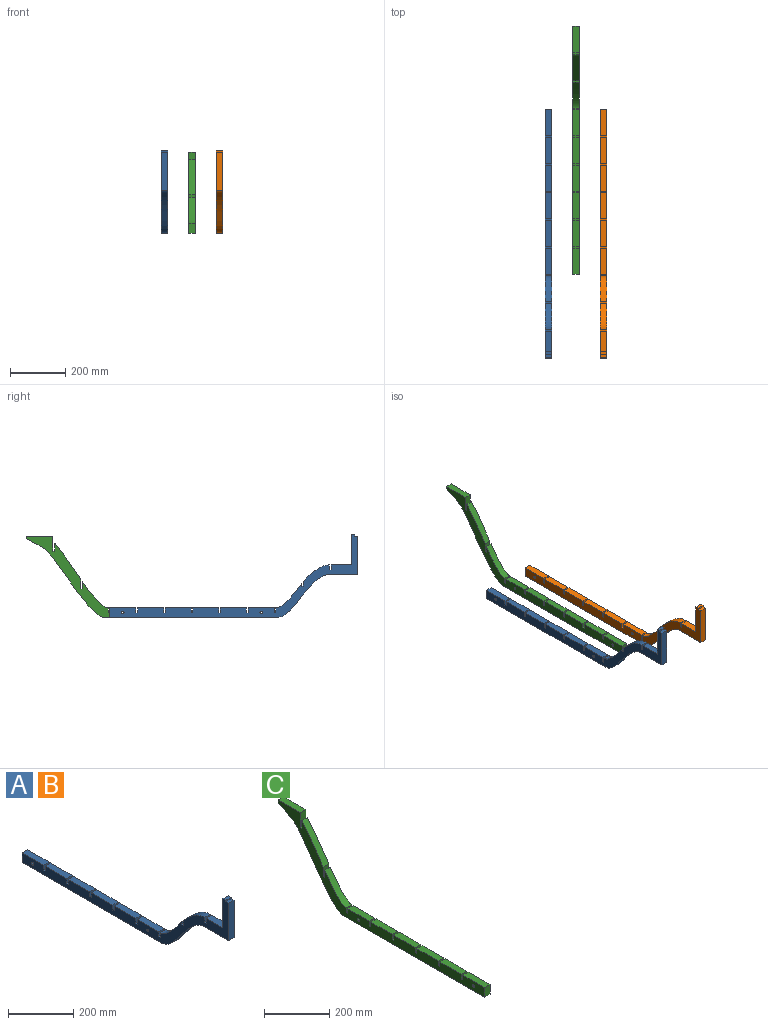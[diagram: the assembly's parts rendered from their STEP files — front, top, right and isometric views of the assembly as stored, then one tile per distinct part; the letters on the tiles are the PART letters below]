
ASSEMBLY  parts=3 mates=4
PART A: 46 faces, bbox 24x897x300 mm
  f0: plane 602.68x24mm, normal (0,0,-1), area 14464.3mm2, adj f1,f42,f44,f45
  f1: plane 36x24mm, normal (0,1,0), area 864mm2, adj f0,f2,f44,f45
  f2: plane 94x24mm, normal (0,0,1), area 2256mm2, adj f1,f3,f44,f45
  f3: plane 24x18mm, normal (0,-1,0), area 432mm2, adj f2,f4,f44,f45
  f4: plane 24x6mm, normal (0,0,1), area 144mm2, adj f3,f5,f44,f45
  f5: plane 24x18mm, normal (0,1,0), area 432mm2, adj f4,f6,f44,f45
  f6: plane 94x24mm, normal (0,0,1), area 2256mm2, adj f5,f7,f44,f45
  f7: plane 24x18mm, normal (0,-1,0), area 432mm2, adj f6,f8,f44,f45
  f8: plane 24x6mm, normal (0,0,1), area 144mm2, adj f7,f9,f44,f45
  f9: plane 24x18mm, normal (0,1,0), area 432mm2, adj f8,f10,f44,f45
  f10: plane 94x24mm, normal (0,0,1), area 2256mm2, adj f9,f11,f44,f45
  f11: plane 24x18mm, normal (0,-1,0), area 432mm2, adj f10,f12,f44,f45
  f12: plane 24x6mm, normal (0,0,1), area 144mm2, adj f11,f13,f44,f45
  f13: plane 24x18mm, normal (0,1,0), area 432mm2, adj f12,f14,f44,f45
  f14: plane 94x24mm, normal (0,0,1), area 2256mm2, adj f13,f15,f44,f45
  f15: plane 24x18mm, normal (0,-1,0), area 432mm2, adj f14,f16,f44,f45
  f16: plane 24x6mm, normal (0,0,1), area 144mm2, adj f15,f17,f44,f45
  f17: plane 24x18mm, normal (0,1,0), area 432mm2, adj f16,f18,f44,f45
  f18: plane 94x24mm, normal (0,0,1), area 2256mm2, adj f17,f19,f44,f45
  f19: plane 24x18mm, normal (0,-1,0), area 432mm2, adj f18,f20,f44,f45
  f20: plane 24x6mm, normal (0,0,1), area 144mm2, adj f19,f21,f44,f45
  f21: plane 24x18mm, normal (0,1,0), area 432mm2, adj f20,f22,f44,f45
  f22: plane 94x24mm, normal (0,0,1), area 2256mm2, adj f21,f23,f44,f45
  f23: plane 24x18mm, normal (0,-1,0), area 432mm2, adj f22,f24,f44,f45
  f24: plane 24x6mm, normal (0,0,1), area 144mm2, adj f23,f25,f44,f45
  f25: plane 24x18mm, normal (0,1,0), area 432mm2, adj f24,f26,f44,f45
  f26: extruded ~94x87.93mm, area 3171.6mm2, adj f25,f27,f44,f45
  f27: plane 24x10.86mm, normal (0,-1,0), area 260.7mm2, adj f26,f28,f44,f45
  f28: plane 24x6mm, normal (0,0,1), area 144mm2, adj f27,f29,f44,f45
  f29: plane 24x18mm, normal (0,1,0), area 432mm2, adj f28,f30,f44,f45
  f30: extruded ~94x58.98mm, area 2735mm2, adj f29,f31,f44,f45
  f31: plane 24x18mm, normal (0,-1,0), area 432mm2, adj f30,f32,f44,f45
  f32: plane 24x6mm, normal (0,0,1), area 144mm2, adj f31,f33,f44,f45
  f33: plane 24x18mm, normal (0,1,0), area 432mm2, adj f32,f34,f44,f45
  f34: plane 73x24mm, normal (0,0,1), area 1752mm2, adj f33,f35,f44,f45
  f35: plane 110x24mm, normal (0,1,0), area 2640mm2, adj f34,f36,f44,f45
  f36: plane 24x12mm, normal (0,0,1), area 288mm2, adj f35,f37,f44,f45
  f37: plane 24x6mm, normal (0,-1,0), area 144mm2, adj f36,f38,f44,f45
  f38: plane 24x12mm, normal (0,0,1), area 288mm2, adj f37,f39,f44,f45
  f39: plane 140x24mm, normal (0,-1,0), area 3360mm2, adj f38,f40,f44,f45
  f40: plane 109.33x24mm, normal (0,0,-1), area 2623.9mm2, adj f39,f42,f44,f45
  f41: cylinder r=4.5mm len=24mm, axis (-1,0,0), area 678.6mm2, adj f44,f45
  f42: extruded ~184.99x154mm, area 5957.9mm2, adj f0,f40,f44,f45
  f43: cylinder r=4.5mm len=24mm, axis (-1,0,0), area 678.6mm2, adj f44,f45
  f44: plane 897x300mm, normal (1,0,0), area 35008.7mm2, adj f0,f1,f2,f3,f4,f5,f6,f7
  f45: plane 897x300mm, normal (-1,0,0), area 35008.7mm2, adj f0,f1,f2,f3,f4,f5,f6,f7
PART B: same geometry as A
PART C: 41 faces, bbox 24x897x294 mm
  f0: plane 24x6mm, normal (0,0,1), area 144mm2, adj f1,f37,f39,f40
  f1: plane 24x18mm, normal (0,1,0), area 432mm2, adj f0,f2,f39,f40
  f2: plane 94x24mm, normal (0,0,1), area 2256mm2, adj f1,f3,f39,f40
  f3: plane 24x18mm, normal (0,-1,0), area 432mm2, adj f2,f4,f39,f40
  f4: plane 24x6mm, normal (0,0,1), area 144mm2, adj f3,f5,f39,f40
  f5: plane 24x18mm, normal (0,1,0), area 432mm2, adj f4,f6,f39,f40
  f6: plane 94x24mm, normal (0,0,1), area 2256mm2, adj f5,f7,f39,f40
  f7: plane 24x18mm, normal (0,-1,0), area 432mm2, adj f6,f8,f39,f40
  f8: plane 24x6mm, normal (0,0,1), area 144mm2, adj f7,f9,f39,f40
  f9: plane 24x18mm, normal (0,1,0), area 432mm2, adj f8,f10,f39,f40
  f10: plane 94x24mm, normal (0,0,1), area 2256mm2, adj f9,f11,f39,f40
  f11: plane 24x18mm, normal (0,-1,0), area 432mm2, adj f10,f12,f39,f40
  f12: plane 24x6mm, normal (0,0,1), area 144mm2, adj f11,f13,f39,f40
  f13: plane 24x18mm, normal (0,1,0), area 432mm2, adj f12,f14,f39,f40
  f14: plane 94x24mm, normal (0,0,1), area 2256mm2, adj f13,f15,f39,f40
  f15: plane 24x18mm, normal (0,-1,0), area 432mm2, adj f14,f16,f39,f40
  f16: plane 24x6mm, normal (0,0,1), area 144mm2, adj f15,f17,f39,f40
  f17: plane 24x18mm, normal (0,1,0), area 432mm2, adj f16,f18,f39,f40
  f18: plane 94x24mm, normal (0,0,1), area 2256mm2, adj f17,f19,f39,f40
  f19: plane 24x18mm, normal (0,-1,0), area 432mm2, adj f18,f20,f39,f40
  f20: plane 24x6mm, normal (0,0,1), area 144mm2, adj f19,f21,f39,f40
  f21: plane 24x18mm, normal (0,1,0), area 432mm2, adj f20,f22,f39,f40
  f22: plane 94x24mm, normal (0,0,1), area 2256mm2, adj f21,f23,f39,f40
  f23: plane 36x24mm, normal (0,-1,0), area 864mm2, adj f22,f24,f39,f40
  f24: plane 609.81x24mm, normal (0,0,-1), area 14635.5mm2, adj f23,f25,f39,f40
  f25: extruded ~287.19x284mm, area 9906mm2, adj f24,f26,f39,f40
  f26: plane 24x10mm, normal (0,1,0), area 240mm2, adj f25,f27,f39,f40
  f27: plane 97x24mm, normal (0,0,1), area 2328mm2, adj f26,f28,f39,f40
  f28: plane 54.17x24mm, normal (0,-1,0), area 1300.2mm2, adj f27,f29,f39,f40
  f29: plane 24x6mm, normal (0,0,1), area 144mm2, adj f28,f30,f39,f40
  f30: plane 27.09x24mm, normal (0,1,0), area 650.1mm2, adj f29,f31,f39,f40
  f31: extruded ~127.19x94mm, area 3806.4mm2, adj f30,f32,f39,f40
  f32: plane 35.36x24mm, normal (0,-1,0), area 848.7mm2, adj f31,f33,f39,f40
  f33: plane 24x6mm, normal (0,0,1), area 144mm2, adj f32,f34,f39,f40
  f34: plane 26.47x24mm, normal (0,1,0), area 635.3mm2, adj f33,f35,f39,f40
  f35: extruded ~94.84x94mm, area 3273.2mm2, adj f34,f37,f39,f40
  f36: cylinder r=4.5mm len=24mm, axis (-1,0,0), area 678.6mm2, adj f39,f40
  f37: plane 24x18mm, normal (0,-1,0), area 432mm2, adj f0,f35,f39,f40
  f38: cylinder r=4.5mm len=24mm, axis (-1,0,0), area 678.6mm2, adj f39,f40
  f39: plane 897x294mm, normal (1,0,0), area 35469.8mm2, adj f0,f1,f2,f3,f4,f5,f6,f7
  f40: plane 897x294mm, normal (-1,0,0), area 35469.8mm2, adj f0,f1,f2,f3,f4,f5,f6,f7
PLACE A t=(-110.81,-1.24,4.59)mm
PLACE B t=(87.19,-1.24,4.59)mm
PLACE C t=(-11.81,-1.24,4.59)mm fixed
MATE fastened A.f43 <-> C.f38  axis (1,0,0) through (-86.81,-851.24,-277.41)mm
MATE fastened C.f38 <-> B.f43  axis (1,0,0) through (12.19,-851.24,-277.41)mm
MATE fastened C.f36 <-> B.f41  axis (1,0,0) through (12.19,-351.24,-277.41)mm
MATE fastened A.f41 <-> C.f36  axis (1,0,0) through (-86.81,-351.24,-277.41)mm
